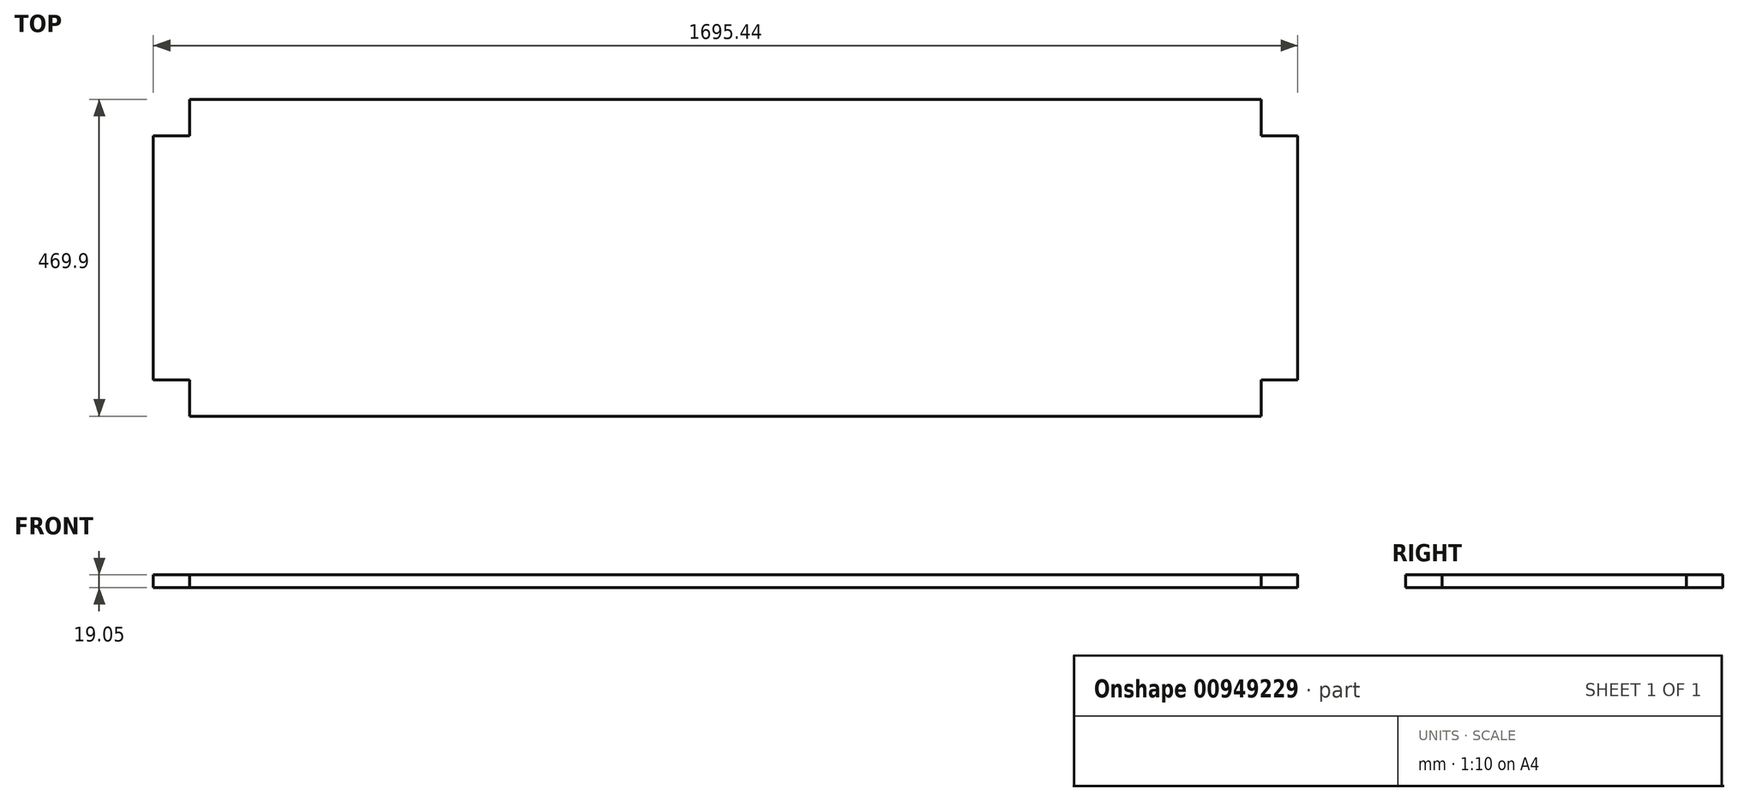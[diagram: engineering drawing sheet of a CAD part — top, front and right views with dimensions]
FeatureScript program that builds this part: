
annotation { "Feature Type Name" : "Feature", "Feature Type Description" : "" }
export const myFeature = defineFeature(function(context is Context, id is Id, definition is map)
    precondition{}
    {
        {
            var Q0;
            Q0=qCreatedBy(makeId("Top.planeOp"),FACE);
            var sketch = newSketch(context, id + "F0", { "sketchPlane" : qUnion([Q0])});
            skLineSegment(sketch, "E0.bottom", {"start": v(-847.72, 234.95) * mm, "end": v(847.72, 234.95) * mm});
            skLineSegment(sketch, "E0.top", {"start": v(-847.73, -234.95) * mm, "end": v(847.72, -234.95) * mm});
            skLineSegment(sketch, "E0.left", {"start": v(-847.72, 234.95) * mm, "end": v(-847.73, -234.95) * mm});
            skLineSegment(sketch, "E0.right", {"start": v(847.72, 234.95) * mm, "end": v(847.72, -234.95) * mm});
            skPoint(sketch, "E0.middle", {"position": v(0, 0) * mm});
            skSolve(sketch);
        }
        {
            var Q0;
            Q0 = qSketchRegion(id + "F0", true);
            extrude(context, id + "F1", {"entities" : qUnion([Q0]), "depth" : (25.4 * .75) * mm, "offsetDistance" : 25 * mm});
        }
        {
            var Q0;
            Q0=makeQuery(id+"F1.opExtrude","CAP_FACE",FACE,{"disambiguationData":[OSD([sQuery(id+"F0.wireOp",EDGE,"E0.bottom"),sQuery(id+"F0.wireOp",EDGE,"E0.top"),sQuery(id+"F0.wireOp",EDGE,"E0.left"),sQuery(id+"F0.wireOp",EDGE,"E0.right")])],"isStart":false});
            var sketch = newSketch(context, id + "F2", { "sketchPlane" : qUnion([Q0])});
            skLineSegment(sketch, "E1.bottom", {"start": v(-847.72, 234.95) * mm, "end": v(-793.75, 234.95) * mm});
            skLineSegment(sketch, "E1.top", {"start": v(-847.72, 180.97) * mm, "end": v(-793.75, 180.97) * mm});
            skLineSegment(sketch, "E1.left", {"start": v(-847.72, 234.95) * mm, "end": v(-847.72, 180.97) * mm});
            skLineSegment(sketch, "E1.right", {"start": v(-793.75, 234.95) * mm, "end": v(-793.75, 180.97) * mm});
            skLineSegment(sketch, "E2.bottom", {"start": v(-847.73, -234.95) * mm, "end": v(-793.75, -234.95) * mm});
            skLineSegment(sketch, "E2.top", {"start": v(-847.72, -180.98) * mm, "end": v(-793.75, -180.98) * mm});
            skLineSegment(sketch, "E2.left", {"start": v(-847.72, -234.95) * mm, "end": v(-847.72, -180.98) * mm});
            skLineSegment(sketch, "E2.right", {"start": v(-793.75, -234.95) * mm, "end": v(-793.75, -180.98) * mm});
            skLineSegment(sketch, "E3.bottom", {"start": v(847.72, 234.95) * mm, "end": v(793.75, 234.95) * mm});
            skLineSegment(sketch, "E3.top", {"start": v(847.72, 180.97) * mm, "end": v(793.75, 180.97) * mm});
            skLineSegment(sketch, "E3.left", {"start": v(847.72, 234.95) * mm, "end": v(847.72, 180.97) * mm});
            skLineSegment(sketch, "E3.right", {"start": v(793.75, 234.95) * mm, "end": v(793.75, 180.97) * mm});
            skLineSegment(sketch, "E4.bottom", {"start": v(847.72, -234.95) * mm, "end": v(793.75, -234.95) * mm});
            skLineSegment(sketch, "E4.top", {"start": v(847.72, -180.97) * mm, "end": v(793.75, -180.97) * mm});
            skLineSegment(sketch, "E4.left", {"start": v(847.72, -234.95) * mm, "end": v(847.72, -180.97) * mm});
            skLineSegment(sketch, "E4.right", {"start": v(793.75, -234.95) * mm, "end": v(793.75, -180.97) * mm});
            skSolve(sketch);
        }
        {
            var Q0;
            Q0 = qSketchRegion(id + "F2", true);
            extrude(context, id + "F3", {"entities" : qUnion([Q0]), "operationType" : NewBodyOperationType.REMOVE, "endBound" : BoundingType.UP_TO_NEXT, "oppositeDirection" : true, "depth" : 25 * mm, "offsetDistance" : 25 * mm});
        }
    });
